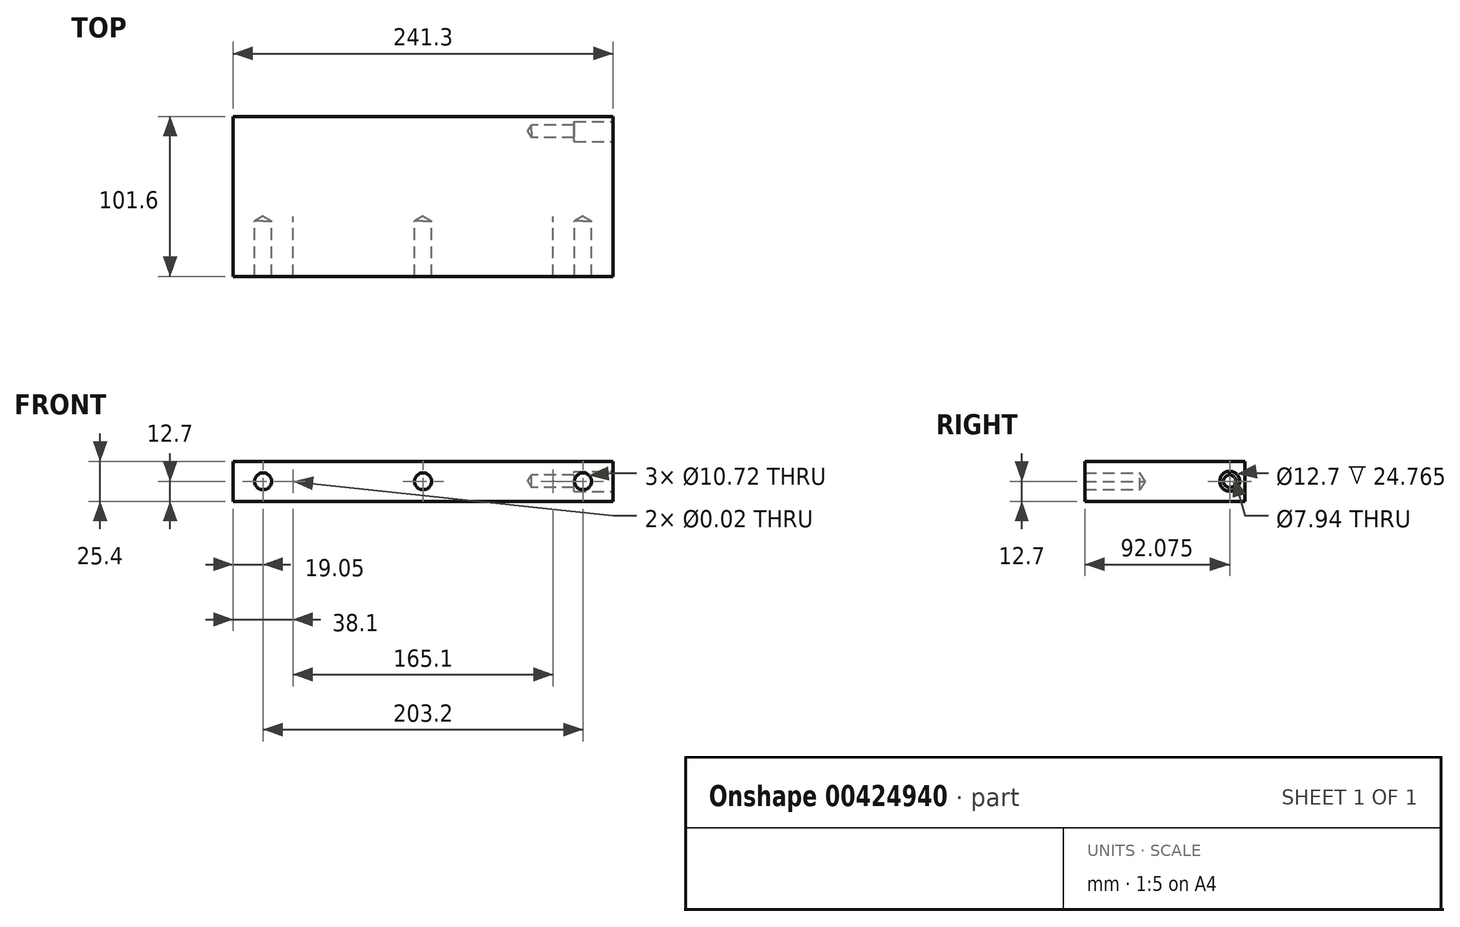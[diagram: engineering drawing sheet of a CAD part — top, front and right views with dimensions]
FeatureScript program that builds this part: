
annotation { "Feature Type Name" : "Feature", "Feature Type Description" : "" }
export const myFeature = defineFeature(function(context is Context, id is Id, definition is map)
    precondition{}
    {
        {
            var Q0;
            Q0=qCreatedBy(makeId("Front.planeOp"),FACE);
            var sketch = newSketch(context, id + "F0", { "sketchPlane" : qUnion([Q0])});
            skLineSegment(sketch, "E0.bottom", {"start": v(120.65, -12.7) * mm, "end": v(-120.65, -12.7) * mm});
            skLineSegment(sketch, "E0.top", {"start": v(120.65, 12.7) * mm, "end": v(-120.65, 12.7) * mm});
            skLineSegment(sketch, "E0.left", {"start": v(120.65, -12.7) * mm, "end": v(120.65, 12.7) * mm});
            skLineSegment(sketch, "E0.right", {"start": v(-120.65, -12.7) * mm, "end": v(-120.65, 12.7) * mm});
            skPoint(sketch, "E0.middle", {"position": v(0, 0) * mm});
            skSolve(sketch);
        }
        {
            var Q0;
            Q0 = qSketchRegion(id + "F0", true);
            extrude(context, id + "F1", {"entities" : qUnion([Q0]), "depth" : 101.6 * mm, "symmetric" : true});
        }
        {
            var Q0;
            Q0=makeQuery(id+"F1.opExtrude","SWEPT_FACE",FACE,{"disambiguationData":[OSD([sQuery(id+"F0.wireOp",EDGE,"E0.left")])]});
            var sketch = newSketch(context, id + "F2", { "sketchPlane" : qUnion([Q0])});
            skCircle(sketch, "E1", {"center": v(41.28, 0) * mm, "radius": 6.35 * mm});
            skPoint(sketch, "E2", {"position": v(50.8, 0) * mm});
            skSolve(sketch);
        }
        {
            var Q0;
            Q0 = qSketchRegion(id + "F2", true);
            extrude(context, id + "F3", {"entities" : qUnion([Q0]), "operationType" : NewBodyOperationType.REMOVE, "oppositeDirection" : true, "depth" : 24.76 * mm});
        }
        {
            var Q0;
            Q0=makeQuery(id+"F3.boolean.opBoolean","COPY",FACE,{"derivedFrom":makeQuery(id+"F3.opExtrude","CAP_FACE",FACE,{"disambiguationData":[OSD([sQuery(id+"F2.wireOp",EDGE,"E1")])],"isStart":false})});
            var sketch = newSketch(context, id + "F4", { "sketchPlane" : qUnion([Q0])});
            skPoint(sketch, "E3", {"position": v(41.28, 0) * mm});
            skSolve(sketch);
        }
        {
            var Q0;
            Q0=sQuery(id+"F4.wireOp",VERTEX,"E3");
            var Q1;
            Q1=makeQuery(id+"F1.opExtrude","SWEPT_BODY",BODY,{"disambiguationData":[OSD([sQuery(id+"F0.wireOp",EDGE,"E0.bottom"),sQuery(id+"F0.wireOp",EDGE,"E0.top"),sQuery(id+"F0.wireOp",EDGE,"E0.left"),sQuery(id+"F0.wireOp",EDGE,"E0.right")])]});
            hole(context, id + "F5", {"style" : HoleStyle.SIMPLE, "endStyle" : HoleEndStyle.BLIND, "standardTappedOrClearance" : lookupTablePath({ "standard" : "ANSI", "engagement" : "75%", "pitch" : "16 tpi", "size" : "3/8", "type" : "Tapped" }), "standardBlindInLast" : lookupTablePath({ "standard" : "ANSI", "engagement" : "75%", "pitch" : "16 tpi", "size" : "3/8", "type" : "Tapped" }), "holeDiameter" : 7.94 * mm, "showTappedDepth" : true, "holeDepth" : 27 * mm, "isTappedThrough" : true, "tappedDepth" : 22.24 * mm, "tapClearance" : 3, "locations" : qUnion([Q0]), "scope" : qUnion([Q1]), "majorDiameter" : 9.53 * mm, "startStyle" : HoleStartStyle.SKETCH});
        }
        {
            var Q0;
            Q0=makeQuery(id+"F1.opExtrude","CAP_FACE",FACE,{"disambiguationData":[OSD([sQuery(id+"F0.wireOp",EDGE,"E0.bottom"),sQuery(id+"F0.wireOp",EDGE,"E0.top"),sQuery(id+"F0.wireOp",EDGE,"E0.left"),sQuery(id+"F0.wireOp",EDGE,"E0.right")])],"isStart":false});
            var sketch = newSketch(context, id + "F6", { "sketchPlane" : qUnion([Q0])});
            skPoint(sketch, "E4", {"position": v(-101.6, 0) * mm});
            skPoint(sketch, "E5", {"position": v(0, 0) * mm});
            skPoint(sketch, "E6", {"position": v(101.6, 0) * mm});
            skPoint(sketch, "E7", {"position": v(-82.55, 0) * mm});
            skPoint(sketch, "E8", {"position": v(82.55, 0) * mm});
            skSolve(sketch);
        }
        {
            var Q0;
            Q0=sQuery(id+"F6.wireOp",VERTEX,"E4");
            var Q1;
            Q1=sQuery(id+"F6.wireOp",VERTEX,"E5");
            var Q2;
            Q2=sQuery(id+"F6.wireOp",VERTEX,"E6");
            var Q3;
            Q3=makeQuery(id+"F1.opExtrude","SWEPT_BODY",BODY,{"disambiguationData":[OSD([sQuery(id+"F0.wireOp",EDGE,"E0.bottom"),sQuery(id+"F0.wireOp",EDGE,"E0.top"),sQuery(id+"F0.wireOp",EDGE,"E0.left"),sQuery(id+"F0.wireOp",EDGE,"E0.right")])]});
            hole(context, id + "F7", {"style" : HoleStyle.SIMPLE, "endStyle" : HoleEndStyle.BLIND, "standardTappedOrClearance" : lookupTablePath({ "standard" : "ANSI", "engagement" : "75%", "pitch" : "13 tpi", "size" : "1/2", "type" : "Tapped" }), "standardBlindInLast" : lookupTablePath({ "standard" : "ANSI", "engagement" : "75%", "pitch" : "13 tpi", "size" : "1/2", "type" : "Tapped" }), "holeDiameter" : 10.72 * mm, "showTappedDepth" : true, "holeDepth" : 35.18 * mm, "isTappedThrough" : true, "tappedDepth" : 29.32 * mm, "tapClearance" : 3, "locations" : qUnion([Q0, Q1, Q2]), "scope" : qUnion([Q3]), "majorDiameter" : 12.7 * mm, "startStyle" : HoleStartStyle.SKETCH});
        }
        {
            var Q0;
            Q0=sQuery(id+"F6.wireOp",VERTEX,"E7");
            var Q1;
            Q1=sQuery(id+"F6.wireOp",VERTEX,"E8");
            var Q2;
            Q2=makeQuery(id+"F1.opExtrude","SWEPT_BODY",BODY,{"disambiguationData":[OSD([sQuery(id+"F0.wireOp",EDGE,"E0.bottom"),sQuery(id+"F0.wireOp",EDGE,"E0.top"),sQuery(id+"F0.wireOp",EDGE,"E0.left"),sQuery(id+"F0.wireOp",EDGE,"E0.right")])]});
            hole(context, id + "F8", {"style" : HoleStyle.SIMPLE, "endStyle" : HoleEndStyle.BLIND, "standardTappedOrClearance" : lookupTablePath({ "standard" : "ANSI", "size" : "1/2 (0.5)", "type" : "Drilled" }), "standardBlindInLast" : lookupTablePath({ "standard" : "ANSI", "size" : "1/2", "type" : "Drilled" }), "holeDiameter" : 1 / 50.8 * mm, "holeDepth" : 38.1 * mm, "isTappedThrough" : true, "tappedDepth" : 29.32 * mm, "tapClearance" : 3, "locations" : qUnion([Q0, Q1]), "scope" : qUnion([Q2]), "startStyle" : HoleStartStyle.SKETCH});
        }
    });
